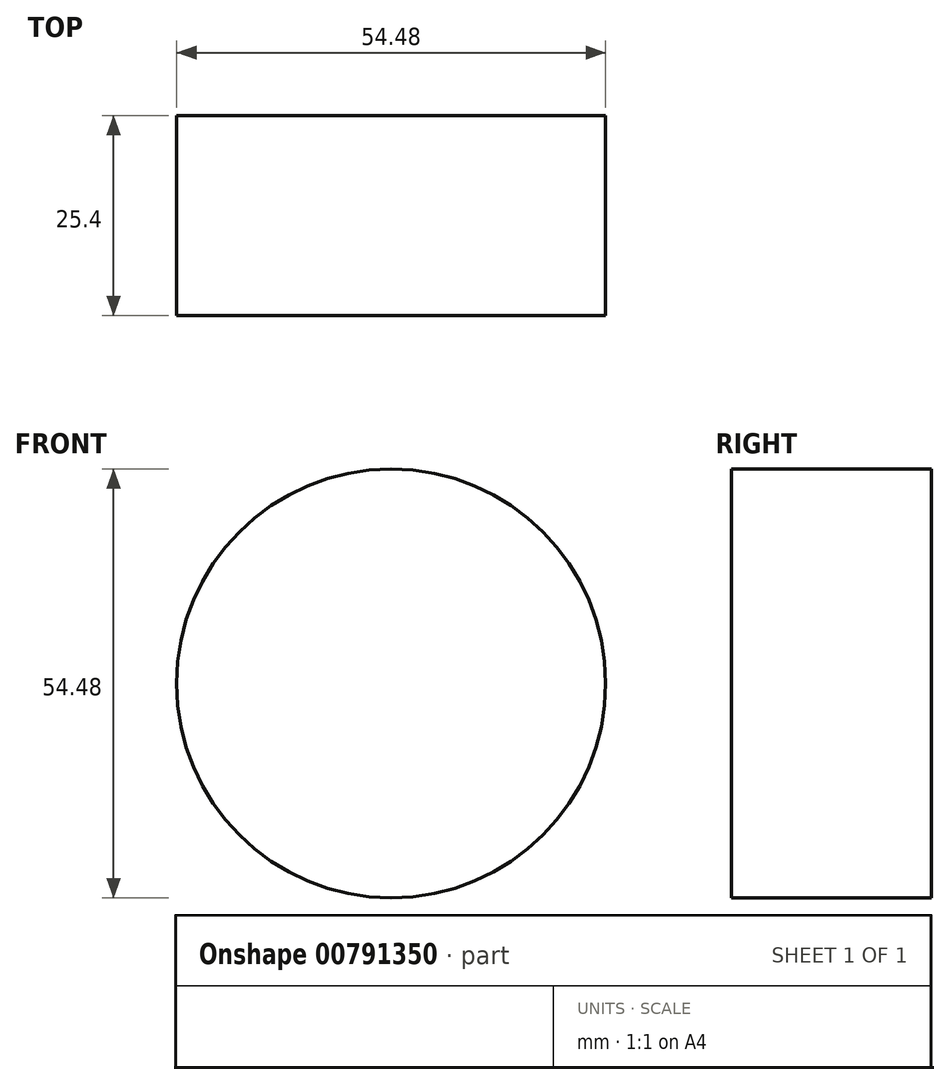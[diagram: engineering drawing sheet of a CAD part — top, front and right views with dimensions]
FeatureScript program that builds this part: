
annotation { "Feature Type Name" : "Feature", "Feature Type Description" : "" }
export const myFeature = defineFeature(function(context is Context, id is Id, definition is map)
    precondition{}
    {
        {
            var Q0;
            Q0=qCreatedBy(makeId("Front.planeOp"),FACE);
            var sketch = newSketch(context, id + "F0", { "sketchPlane" : qUnion([Q0])});
            skCircle(sketch, "E0", {"center": v(0, 0) * mm, "radius": 27.24 * mm});
            skSolve(sketch);
        }
        {
            var Q0;
            Q0=makeQuery(id+"F0.imprint","IMPRINT",FACE,{"disambiguationData":[TD([[makeQuery(id+"F0.imprint","IMPRINT",EDGE,{"derivedFrom":sQuery(id+"F0.wireOp",EDGE,"E0")}),1.0]])]});
            extrude(context, id + "F1", {"entities" : qUnion([Q0]), "endBound" : BoundingType.SYMMETRIC, "depth" : 25.4 * mm, "offsetDistance" : 25.4 * mm});
        }
    });
